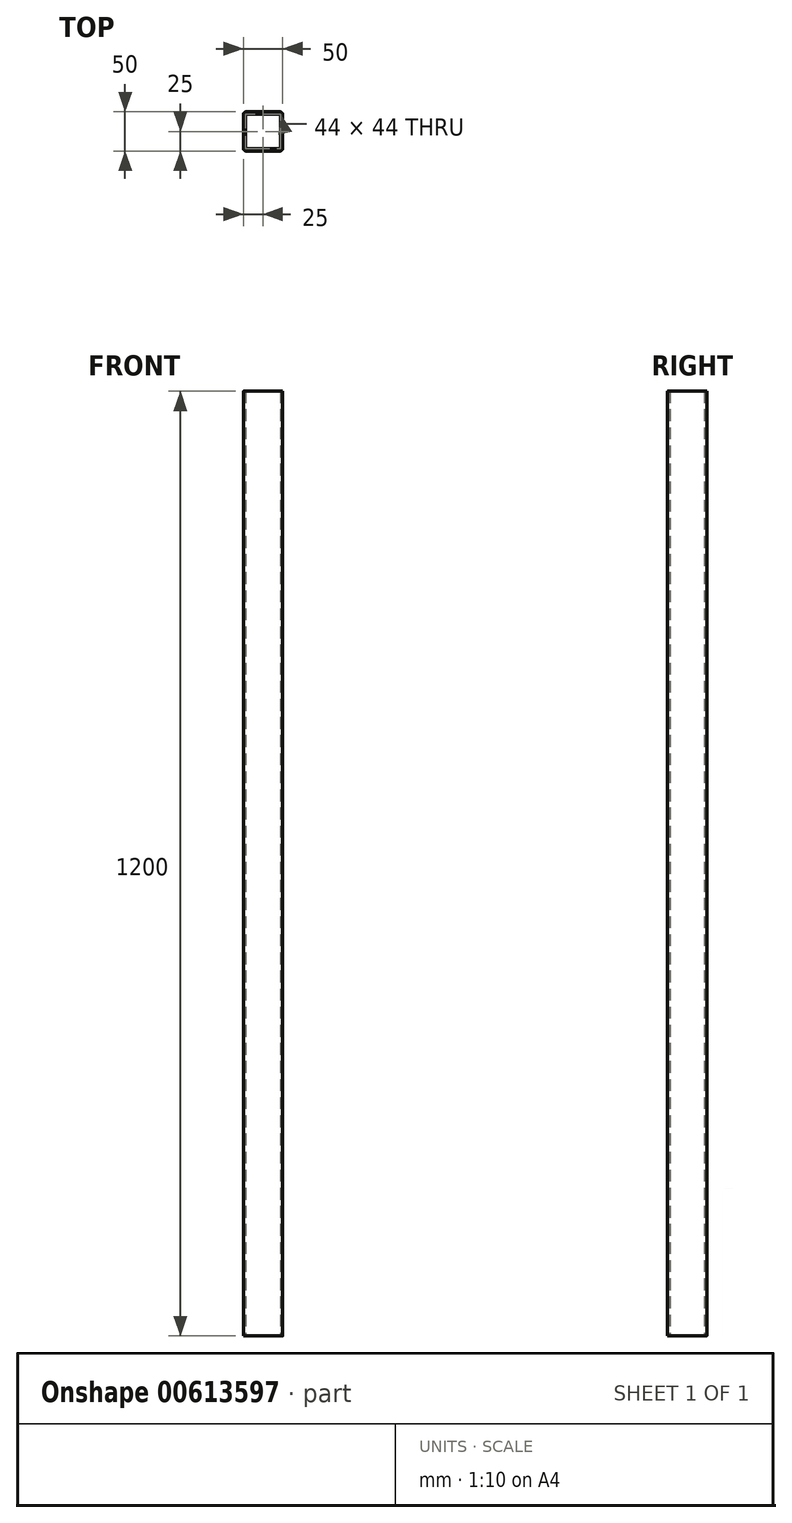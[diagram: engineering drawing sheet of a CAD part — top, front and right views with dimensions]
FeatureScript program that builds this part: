
annotation { "Feature Type Name" : "Feature", "Feature Type Description" : "" }
export const myFeature = defineFeature(function(context is Context, id is Id, definition is map)
    precondition{}
    {
        {
            var Q0;
            Q0=qCreatedBy(makeId("Top.planeOp"),FACE);
            var sketch = newSketch(context, id + "F0", { "sketchPlane" : qUnion([Q0])});
            skLineSegment(sketch, "E0.bottom", {"start": v(4, 0) * mm, "end": v(46, 0) * mm});
            skLineSegment(sketch, "E0.top", {"start": v(4, 50) * mm, "end": v(46, 50) * mm});
            skLineSegment(sketch, "E0.left", {"start": v(0, 4) * mm, "end": v(0, 46) * mm});
            skLineSegment(sketch, "E0.right", {"start": v(50, 4) * mm, "end": v(50, 46) * mm});
            skPoint(sketch, "E1.visualSharp", {"position": v(50, 0) * mm});
            skArc(sketch, "E1.filletArc", {"start": v(46, 0) * mm, "mid": v(48.83, 1.17) * mm, "end": v(50, 4) * mm});
            skPoint(sketch, "E2.visualSharp", {"position": v(50, 50) * mm});
            skArc(sketch, "E2.filletArc", {"start": v(50, 46) * mm, "mid": v(48.83, 48.83) * mm, "end": v(46, 50) * mm});
            skPoint(sketch, "E3.visualSharp", {"position": v(0, 50) * mm});
            skArc(sketch, "E3.filletArc", {"start": v(4, 50) * mm, "mid": v(1.17, 48.83) * mm, "end": v(0, 46) * mm});
            skPoint(sketch, "E4.visualSharp", {"position": v(0, 0) * mm});
            skArc(sketch, "E4.filletArc", {"start": v(0, 4) * mm, "mid": v(1.17, 1.17) * mm, "end": v(4, 0) * mm});
            skLineSegment(sketch, "E5.0", {"start": v(3, 47) * mm, "end": v(47, 47) * mm});
            skLineSegment(sketch, "E5.1", {"start": v(3, 3) * mm, "end": v(3, 47) * mm});
            skLineSegment(sketch, "E5.2", {"start": v(3, 3) * mm, "end": v(47, 3) * mm});
            skLineSegment(sketch, "E5.3", {"start": v(47, 3) * mm, "end": v(47, 47) * mm});
            skSolve(sketch);
        }
        {
            var Q0;
            Q0=qSketchRegion(id+"F0",true);
            extrude(context, id + "F1", {"entities" : qUnion([Q0]), "depth" : 1200 * mm, "offsetDistance" : 25 * mm});
        }
    });
